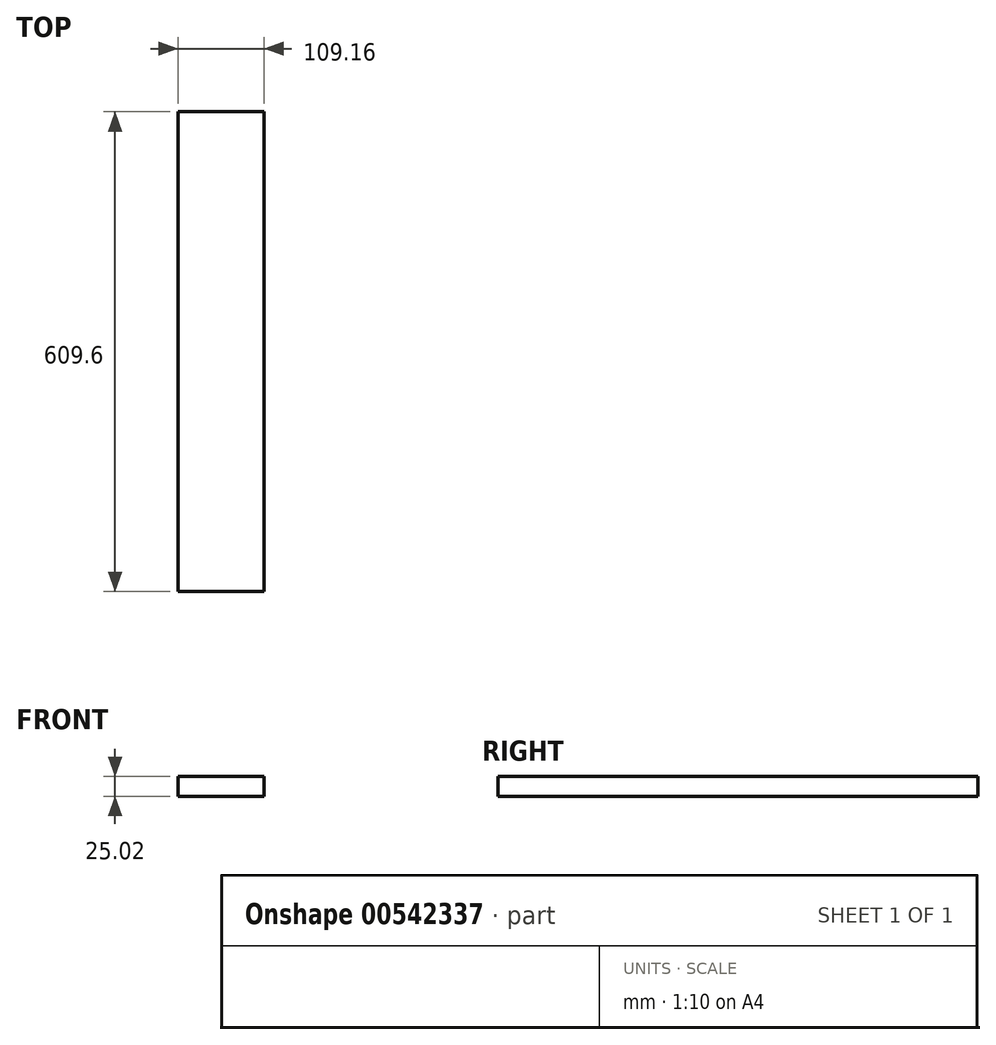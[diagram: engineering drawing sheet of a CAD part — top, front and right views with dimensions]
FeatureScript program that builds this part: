
annotation { "Feature Type Name" : "Feature", "Feature Type Description" : "" }
export const myFeature = defineFeature(function(context is Context, id is Id, definition is map)
    precondition{}
    {
        {
            var Q0;
            Q0=qCreatedBy(makeId("Front.planeOp"),FACE);
            var sketch = newSketch(context, id + "F0", { "sketchPlane" : qUnion([Q0])});
            skLineSegment(sketch, "E0.bottom", {"start": v(-54.58, -12.5) * mm, "end": v(54.58, -12.5) * mm});
            skLineSegment(sketch, "E0.top", {"start": v(-54.58, 12.5) * mm, "end": v(54.58, 12.5) * mm});
            skLineSegment(sketch, "E0.left", {"start": v(-54.58, -12.5) * mm, "end": v(-54.58, 12.5) * mm});
            skLineSegment(sketch, "E0.right", {"start": v(54.58, -12.5) * mm, "end": v(54.58, 12.5) * mm});
            skPoint(sketch, "E0.middle", {"position": v(0, 0) * mm});
            skSolve(sketch);
        }
        {
            var Q0;
            Q0 = qSketchRegion(id + "F0", true);
            extrude(context, id + "F1", {"entities" : qUnion([Q0]), "depth" : 609.6 * mm, "offsetDistance" : 25.4 * mm});
        }
    });
